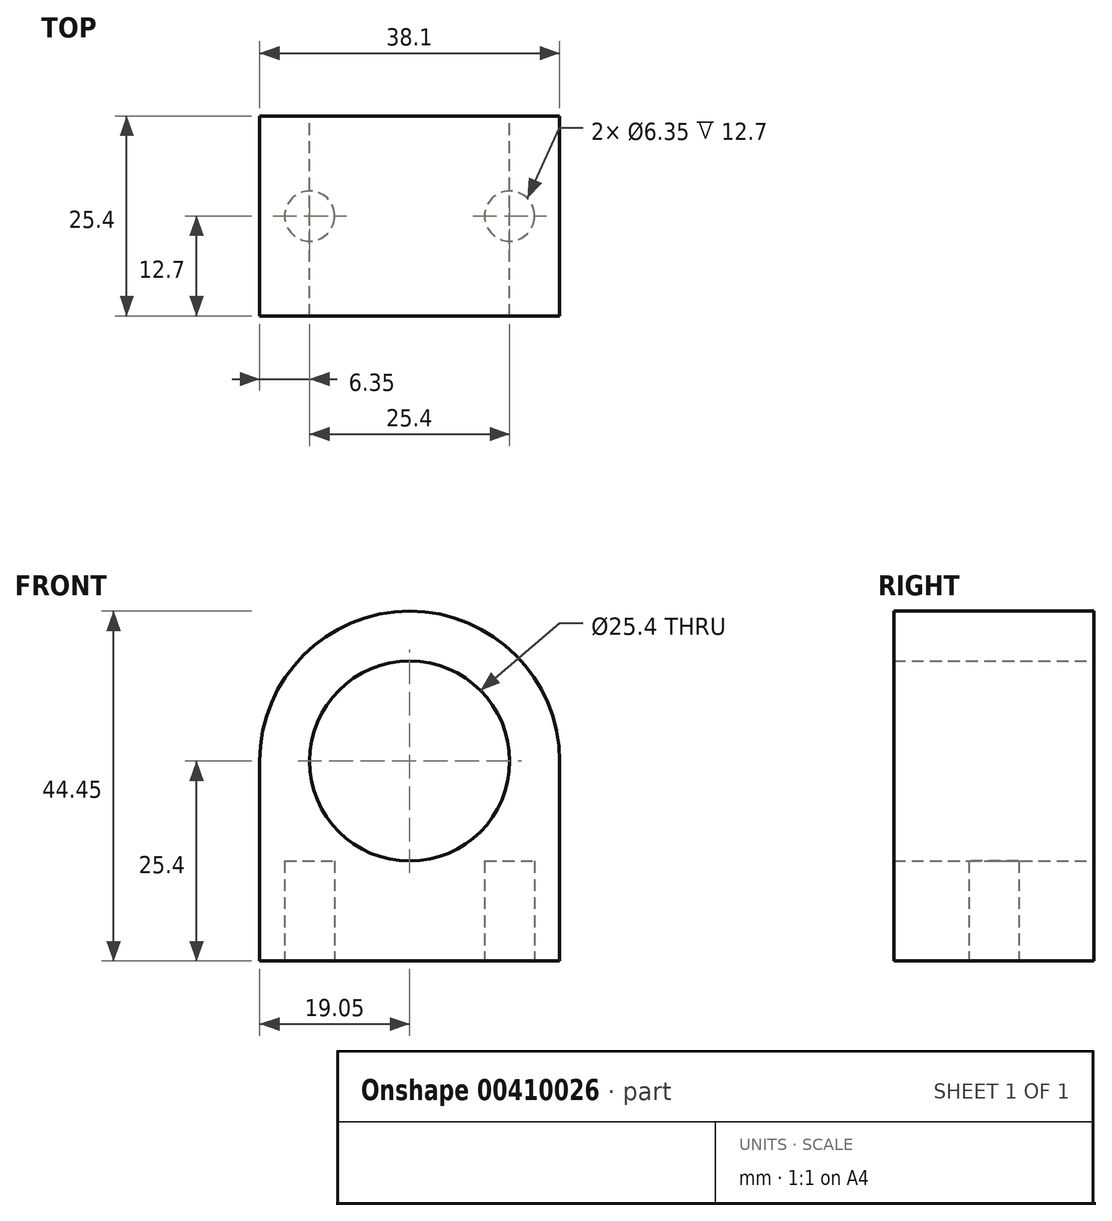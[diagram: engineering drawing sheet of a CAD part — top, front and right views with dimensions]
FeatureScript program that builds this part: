
annotation { "Feature Type Name" : "Feature", "Feature Type Description" : "" }
export const myFeature = defineFeature(function(context is Context, id is Id, definition is map)
    precondition{}
    {
        {
            var Q0;
            Q0=qCreatedBy(makeId("Front.planeOp"),FACE);
            var sketch = newSketch(context, id + "F0", { "sketchPlane" : qUnion([Q0])});
            skCircle(sketch, "E0", {"center": v(0, 0) * mm, "radius": 12.7 * mm});
            skArc(sketch, "E1", {"start": v(19.05, 0) * mm, "mid": v(0, 19.05) * mm, "end": v(-19.05, 0) * mm});
            skLineSegment(sketch, "E2", {"start": v(-19.05, 0) * mm, "end": v(-19.05, -25.4) * mm});
            skLineSegment(sketch, "E3", {"start": v(-19.05, -25.4) * mm, "end": v(19.05, -25.4) * mm});
            skLineSegment(sketch, "E4", {"start": v(19.05, -25.4) * mm, "end": v(19.05, 0) * mm});
            skSolve(sketch);
        }
        {
            var Q0;
            Q0 = qSketchRegion(id + "F0", true);
            extrude(context, id + "F1", {"entities" : qUnion([Q0]), "depth" : 25.4 * mm});
        }
        {
            var Q0;
            Q0=makeQuery(id+"F1.opExtrude","SWEPT_FACE",FACE,{"disambiguationData":[OSD([sQuery(id+"F0.wireOp",EDGE,"E3")])]});
            var sketch = newSketch(context, id + "F2", { "sketchPlane" : qUnion([Q0])});
            skLineSegment(sketch, "E5", {"start": v(-18.73, 12.7) * mm, "end": v(48.56, 12.7) * mm, "construction": true});
            skCircle(sketch, "E6", {"center": v(-12.7, 12.7) * mm, "radius": 3.18 * mm});
            skCircle(sketch, "E7.MirrorC", {"center": v(12.7, 12.7) * mm, "radius": 3.18 * mm});
            skSolve(sketch);
        }
        {
            var Q0;
            Q0 = qSketchRegion(id + "F2", true);
            extrude(context, id + "F3", {"entities" : qUnion([Q0]), "operationType" : NewBodyOperationType.REMOVE, "oppositeDirection" : true, "depth" : 12.7 * mm});
        }
    });
